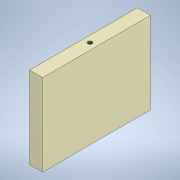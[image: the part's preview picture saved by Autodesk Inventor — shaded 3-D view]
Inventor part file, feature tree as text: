
AUTODESK INVENTOR PART (.ipt)
format: ipt  version: 2020 (Build 240168000, 168)  size: 100,352 bytes
history: native  units: mm
features: extrude x1, hole x1, sketch x1
ambient origin geometry x8: Origin, YZ Plane, XZ Plane, XY Plane, X Axis, Y Axis, Z Axis, Center Point
bodies: Solid1 (feature_tree)
feature tree (3):
  extrude  "Extrusion1"  Depth=63.0mm
  hole  "Hole1"  [1 undecoded]
  sketch  "Sketch1"  dims[d0=10.0mm d1=63.0mm d2=82.8mm d3=0.0mm d4=5.0mm d5=41.4mm d6=3.242mm d7=8.0mm d8=4.0mm d9=2.0mm d10=90.0deg d11=12.0mm d12=20.594885mm]
note: 1 required parameter value undecoded (feature->parameter linkage not recoverable at this tier; creation-order binding heuristic only, values carry confidence <= 0.55)
